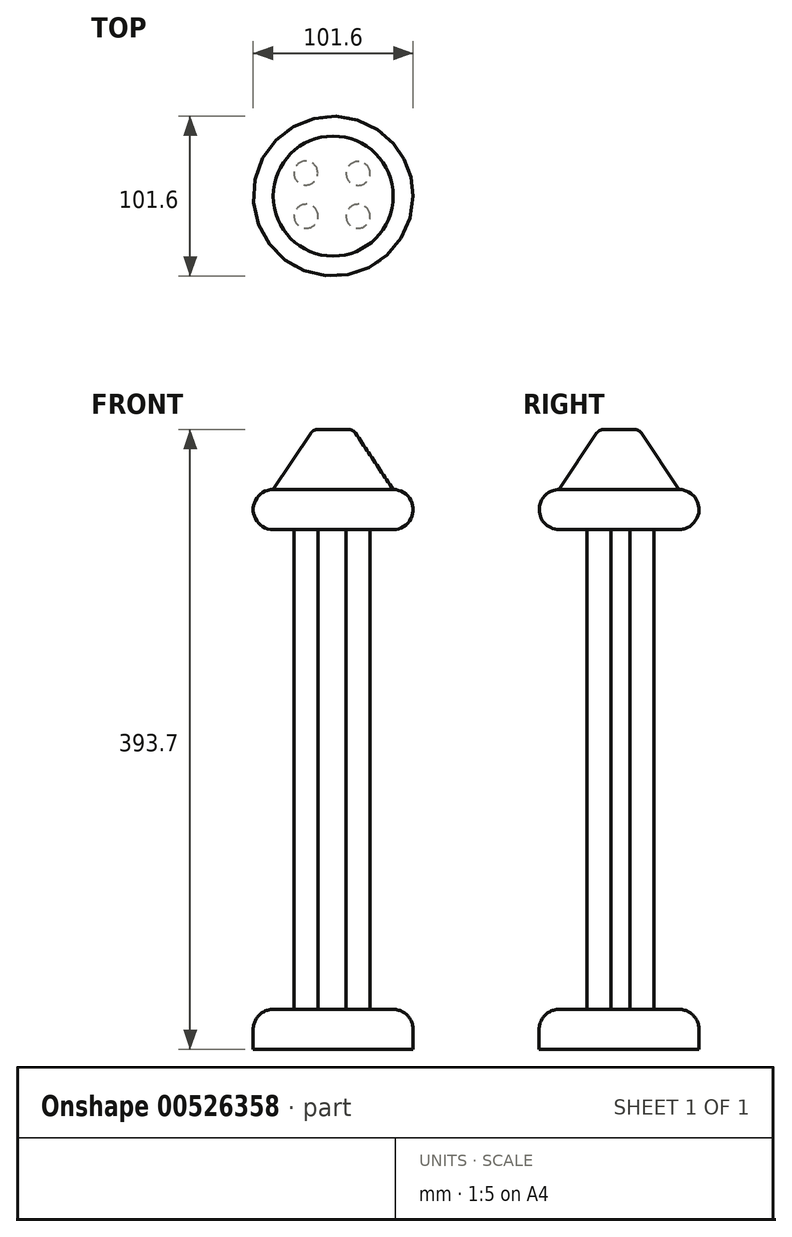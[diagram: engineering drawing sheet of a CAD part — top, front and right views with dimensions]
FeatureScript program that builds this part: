
annotation { "Feature Type Name" : "Feature", "Feature Type Description" : "" }
export const myFeature = defineFeature(function(context is Context, id is Id, definition is map)
    precondition{}
    {
        {
            var Q0;
            Q0=qCreatedBy(makeId("Top.planeOp"),FACE);
            var sketch = newSketch(context, id + "F0", { "sketchPlane" : qUnion([Q0])});
            skCircle(sketch, "E0", {"center": v(0, 0) * mm, "radius": 50.8 * mm});
            skSolve(sketch);
        }
        {
            var Q0;
            Q0=makeQuery(id+"F0.imprint","IMPRINT",FACE,{"disambiguationData":[TD([[makeQuery(id+"F0.imprint","IMPRINT",EDGE,{"derivedFrom":sQuery(id+"F0.wireOp",EDGE,"E0")}),1.0]])]});
            extrude(context, id + "F1", {"entities" : qUnion([Q0]), "depth" : 25.4 * mm, "offsetDistance" : 25.4 * mm});
        }
        {
            var Q0;
            Q0=makeQuery(id+"F1.opExtrude","CAP_EDGE",EDGE,{"disambiguationData":[OSD([sQuery(id+"F0.wireOp",EDGE,"E0")])],"isStart":false});
            fillet(context, id + "F2", {"entities" : qUnion([Q0]), "radius" : 12.7 * mm, "tangentPropagation" : true, "allowEdgeOverflow" : false});
        }
        {
            var Q0;
            Q0=makeQuery(id+"F1.opExtrude","CAP_FACE",FACE,{"disambiguationData":[OSD([sQuery(id+"F0.wireOp",EDGE,"E0")])],"isStart":false});
            var sketch = newSketch(context, id + "F3", { "sketchPlane" : qUnion([Q0])});
            skCircle(sketch, "E1", {"center": v(-17.38, 14.65) * mm, "radius": 7.62 * mm});
            skSolve(sketch);
        }
        {
            var Q0;
            Q0=makeQuery(id+"F3.imprint","IMPRINT",FACE,{"disambiguationData":[TD([[makeQuery(id+"F3.imprint","IMPRINT",EDGE,{"derivedFrom":sQuery(id+"F3.wireOp",EDGE,"E1")}),-1.0]])]});
            var sketch = newSketch(context, id + "F4", { "sketchPlane" : qUnion([Q0])});
            skCircle(sketch, "E2", {"center": v(15.82, 14.4) * mm, "radius": 7.62 * mm});
            skCircle(sketch, "E3", {"center": v(-17.12, -12.84) * mm, "radius": 7.62 * mm});
            skCircle(sketch, "E4", {"center": v(15.82, -12.84) * mm, "radius": 7.62 * mm});
            skSolve(sketch);
        }
        {
            var Q0;
            Q0=makeQuery(id+"F3.imprint","IMPRINT",FACE,{"disambiguationData":[TD([[makeQuery(id+"F3.imprint","IMPRINT",EDGE,{"derivedFrom":sQuery(id+"F3.wireOp",EDGE,"E1")}),1.0]])]});
            extrude(context, id + "F5", {"entities" : qUnion([Q0]), "operationType" : NewBodyOperationType.ADD, "depth" : 304.8 * mm, "offsetDistance" : 25.4 * mm});
        }
        {
            var Q0;
            Q0=makeQuery(id+"F4.imprint","IMPRINT",FACE,{"disambiguationData":[TD([[makeQuery(id+"F4.imprint","IMPRINT",EDGE,{"derivedFrom":sQuery(id+"F4.wireOp",EDGE,"E2")}),1.0]])]});
            var Q1;
            Q1=makeQuery(id+"F4.imprint","IMPRINT",FACE,{"disambiguationData":[TD([[makeQuery(id+"F4.imprint","IMPRINT",EDGE,{"derivedFrom":sQuery(id+"F4.wireOp",EDGE,"E4")}),1.0]])]});
            var Q2;
            Q2=makeQuery(id+"F4.imprint","IMPRINT",FACE,{"disambiguationData":[TD([[makeQuery(id+"F4.imprint","IMPRINT",EDGE,{"derivedFrom":sQuery(id+"F4.wireOp",EDGE,"E3")}),1.0]])]});
            extrude(context, id + "F6", {"entities" : qUnion([Q0, Q1, Q2]), "operationType" : NewBodyOperationType.ADD, "depth" : 304.8 * mm, "offsetDistance" : 25.4 * mm});
        }
        {
            var Q0;
            Q0=qCreatedBy(makeId("Top.planeOp"),FACE);
            cPlane(context, id + "F7", {"entities" : qUnion([Q0]), "cplaneType" : CPlaneType.OFFSET, "offset" : 330.2 * mm, "width" : 152.4 * mm, "height" : 152.4 * mm});
        }
        {
            var Q0;
            Q0=qCreatedBy(id+"F7.planeOp",FACE);
            var sketch = newSketch(context, id + "F8", { "sketchPlane" : qUnion([Q0])});
            skCircle(sketch, "E5", {"center": v(0, 0) * mm, "radius": 50.8 * mm});
            skSolve(sketch);
        }
        {
            var Q0;
            Q0 = qSketchRegion(id + "F8", true);
            extrude(context, id + "F9", {"entities" : qUnion([Q0]), "operationType" : NewBodyOperationType.ADD, "depth" : 25.4 * mm, "offsetDistance" : 25.4 * mm});
        }
        {
            var Q0;
            Q0=makeQuery(id+"F9.opExtrude","CAP_EDGE",EDGE,{"disambiguationData":[OSD([sQuery(id+"F8.wireOp",EDGE,"E5")])],"isStart":true});
            fillet(context, id + "F10", {"entities" : qUnion([Q0]), "radius" : 12.7 * mm, "tangentPropagation" : true, "allowEdgeOverflow" : false});
        }
        {
            var Q0;
            Q0=makeQuery(id+"F9.opExtrude","CAP_EDGE",EDGE,{"disambiguationData":[OSD([sQuery(id+"F8.wireOp",EDGE,"E5")])],"isStart":false});
            fillet(context, id + "F11", {"entities" : qUnion([Q0]), "radius" : 12.7 * mm, "tangentPropagation" : true, "allowEdgeOverflow" : false});
        }
        {
            var Q0;
            Q0=qCreatedBy(id+"F7.planeOp",FACE);
            cPlane(context, id + "F12", {"entities" : qUnion([Q0]), "cplaneType" : CPlaneType.OFFSET, "offset" : 88.9 * mm, "oppositeDirection" : true, "width" : 152.4 * mm, "height" : 152.4 * mm});
        }
        {
            var Q0;
            Q0=qCreatedBy(id+"F12.planeOp",FACE);
            cPlane(context, id + "F13", {"entities" : qUnion([Q0]), "cplaneType" : CPlaneType.OFFSET, "offset" : 88.9 * mm, "oppositeDirection" : true, "width" : 152.4 * mm, "height" : 152.4 * mm});
        }
        {
            var Q0;
            Q0=qCreatedBy(id+"F13.planeOp",FACE);
            cPlane(context, id + "F14", {"entities" : qUnion([Q0]), "cplaneType" : CPlaneType.OFFSET, "offset" : 88.9 * mm, "oppositeDirection" : true, "width" : 152.4 * mm, "height" : 152.4 * mm});
        }
        {
            var Q0;
            Q0=qCreatedBy(id+"F14.planeOp",FACE);
            var sketch = newSketch(context, id + "F15", { "sketchPlane" : qUnion([Q0])});
            skCircle(sketch, "E6", {"center": v(0, 0) * mm, "radius": 50.8 * mm});
            skSolve(sketch);
        }
        {
            var Q0;
            Q0=sQuery(id+"F15.wireOp",EDGE,"E6");
            extrude(context, id + "F16", {"bodyType" : ToolBodyType.SURFACE, "surfaceEntities" : qUnion([Q0]), "depth" : 25.4 * mm, "offsetDistance" : 25.4 * mm});
        }
        {
            var Q0;
            Q0=qCreatedBy(id+"F13.planeOp",FACE);
            var sketch = newSketch(context, id + "F17", { "sketchPlane" : qUnion([Q0])});
            skCircle(sketch, "E7", {"center": v(0, 0) * mm, "radius": 50.8 * mm});
            skSolve(sketch);
        }
        {
            var Q0;
            Q0=sQuery(id+"F17.wireOp",EDGE,"E7");
            extrude(context, id + "F18", {"bodyType" : ToolBodyType.SURFACE, "surfaceEntities" : qUnion([Q0]), "depth" : 25.4 * mm, "offsetDistance" : 25.4 * mm});
        }
        {
            var Q0;
            Q0=qCreatedBy(id+"F12.planeOp",FACE);
            var sketch = newSketch(context, id + "F19", { "sketchPlane" : qUnion([Q0])});
            skCircle(sketch, "E8", {"center": v(0, 0) * mm, "radius": 50.8 * mm});
            skSolve(sketch);
        }
        {
            var Q0;
            Q0=sQuery(id+"F19.wireOp",EDGE,"E8");
            extrude(context, id + "F20", {"bodyType" : ToolBodyType.SURFACE, "surfaceEntities" : qUnion([Q0]), "depth" : 25.4 * mm, "offsetDistance" : 25.4 * mm});
        }
        {
            var Q0;
            Q0=qCreatedBy(id+"F7.planeOp",FACE);
            cPlane(context, id + "F21", {"entities" : qUnion([Q0]), "cplaneType" : CPlaneType.OFFSET, "offset" : 63.5 * mm, "width" : 152.4 * mm, "height" : 152.4 * mm});
        }
        {
            var Q0;
            Q0=qCreatedBy(id+"F21.planeOp",FACE);
            var sketch = newSketch(context, id + "F22", { "sketchPlane" : qUnion([Q0])});
            skCircle(sketch, "E9", {"center": v(0, 0) * mm, "radius": 12.7 * mm});
            skSolve(sketch);
        }
        {
            var Q1;
            Q1=makeQuery(id+"F9.opExtrude","CAP_FACE",FACE,{"disambiguationData":[OSD([sQuery(id+"F8.wireOp",EDGE,"E5")])],"isStart":false});
            var Q2;
            Q2=makeQuery(id+"F22.imprint","IMPRINT",FACE,{"disambiguationData":[TD([[makeQuery(id+"F22.imprint","IMPRINT",EDGE,{"derivedFrom":sQuery(id+"F22.wireOp",EDGE,"E9")}),1.0]])]});
            loft(context, id + "F23", {"operationType" : NewBodyOperationType.ADD, "sheetProfilesArray" : [{ "sheetProfileEntities" : qUnion([Q1]) }, { "sheetProfileEntities" : qUnion([Q2]) }]});
        }
        {
            var Q0;
            Q0=makeQuery(id+"F23.opLoft","MID_CAP_EDGE",EDGE,{"disambiguationData":[OSD([sQuery(id+"F8.wireOp",EDGE,"E5"),sQuery(id+"F22.wireOp",EDGE,"E9")])],"capPos":1.0});
            fillet(context, id + "F24", {"entities" : qUnion([Q0]), "radius" : 5.08 * mm, "tangentPropagation" : true, "allowEdgeOverflow" : false});
        }
    });
